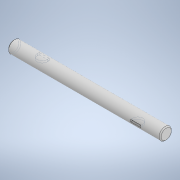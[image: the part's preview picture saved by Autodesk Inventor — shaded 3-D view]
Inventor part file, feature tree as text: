
AUTODESK INVENTOR PART (.ipt)
format: ipt  version: 2021 (Build 250183000, 183)  size: 129,024 bytes
history: native  units: mm
features: other x3, sketch x2, chamfer x1, extrude x1
ambient origin geometry x8: Origin, YZ Plane, XZ Plane, XY Plane, X Axis, Y Axis, Z Axis, Center Point
bodies: Body1 (feature_tree)
feature tree (7):
  other  "Sólido1"
  other  "Revolução1"
  sketch  "Esboço2"  dims[d1=3.0mm d2=90.0deg d3=0.5mm d4=2.0mm d5=45.0deg d6=5.0mm d9=5.0mm d10=12.0mm d11=1.5mm d12=12.0mm d13=1.5mm d14=1.0mm d15=0.0mm d16=0.5mm d17=0.872665mm d18=0.5mm d19=0.872665mm]
  chamfer  "Chanfro1"  Angle=90.0deg  [1 undecoded]
  extrude  "Extrusão1"  Depth=1.0mm TaperAngle=45.0deg
  sketch  "Esboço1"  dims[d0=75.0mm]
  other  "Projetar arestas de corte1"
note: 1 required parameter value undecoded (feature->parameter linkage not recoverable at this tier; creation-order binding heuristic only, values carry confidence <= 0.55)
